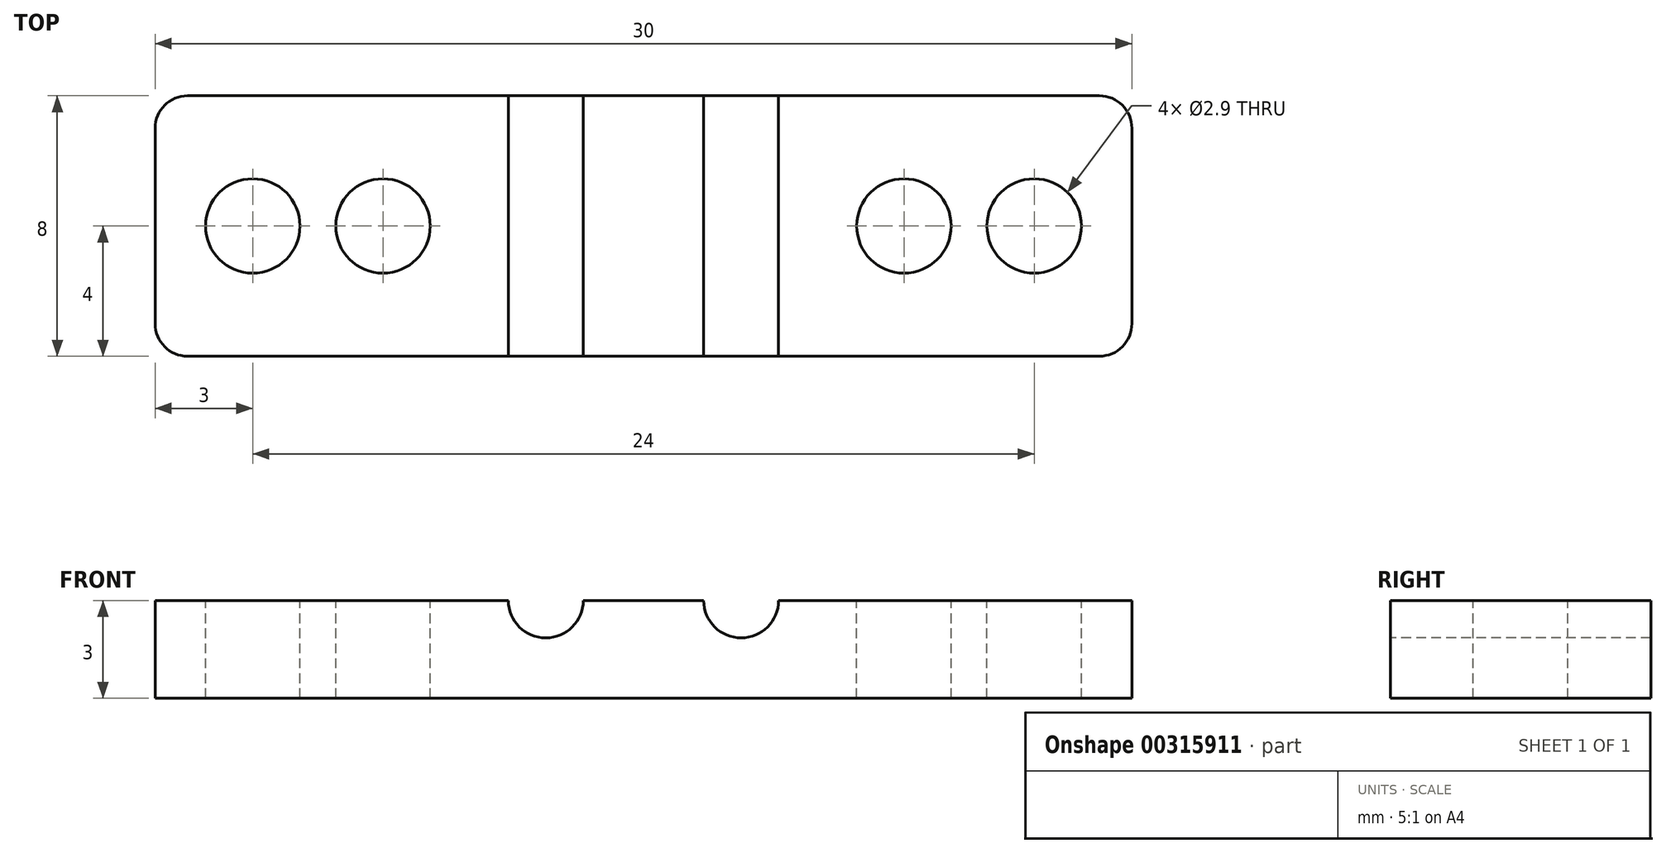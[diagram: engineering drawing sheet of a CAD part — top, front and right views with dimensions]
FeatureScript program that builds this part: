
annotation { "Feature Type Name" : "Feature", "Feature Type Description" : "" }
export const myFeature = defineFeature(function(context is Context, id is Id, definition is map)
    precondition{}
    {
        {
            var Q0;
            Q0=qCreatedBy(makeId("Top.planeOp"),FACE);
            var sketch = newSketch(context, id + "F0", { "sketchPlane" : qUnion([Q0])});
            skLineSegment(sketch, "E0.bottom", {"start": v(3, 4) * mm, "end": v(-3, 4) * mm});
            skLineSegment(sketch, "E0.top", {"start": v(3, -4) * mm, "end": v(-3, -4) * mm});
            skLineSegment(sketch, "E0.left", {"start": v(3, 4) * mm, "end": v(3, -4) * mm});
            skLineSegment(sketch, "E0.right", {"start": v(-3, 4) * mm, "end": v(-3, -4) * mm});
            skPoint(sketch, "E0.middle", {"position": v(0, 0) * mm});
            skLineSegment(sketch, "E1.bottom", {"start": v(27, 4) * mm, "end": v(21, 4) * mm});
            skLineSegment(sketch, "E1.top", {"start": v(27, -4) * mm, "end": v(21, -4) * mm});
            skLineSegment(sketch, "E1.left", {"start": v(27, 4) * mm, "end": v(27, -4) * mm});
            skLineSegment(sketch, "E1.right", {"start": v(21, 4) * mm, "end": v(21, -4) * mm});
            skPoint(sketch, "E1.middle", {"position": v(24, 0) * mm});
            skLineSegment(sketch, "E2", {"start": v(3, 4) * mm, "end": v(21, 4) * mm});
            skLineSegment(sketch, "E3", {"start": v(3, -4) * mm, "end": v(21, -4) * mm});
            skLineSegment(sketch, "E4", {"start": v(9, 4) * mm, "end": v(9, -4) * mm, "construction": true});
            skLineSegment(sketch, "E5.1.0.0", {"start": v(15, 4) * mm, "end": v(15, -4) * mm, "construction": true});
            skLineSegment(sketch, "E5.direction1", {"start": v(9, -4) * mm, "end": v(15, -4) * mm, "construction": true});
            skPoint(sketch, "E6", {"position": v(4, 0) * mm});
            skPoint(sketch, "E6.positionSnap0", {"position": v(3, 0) * mm});
            skPoint(sketch, "E7", {"position": v(20, 0) * mm});
            skPoint(sketch, "E7.positionSnap0", {"position": v(21, 0) * mm});
            skSolve(sketch);
        }
        {
            var Q0;
            Q0=makeQuery(id+"F0.imprint","IMPRINT",FACE,{"disambiguationData":[TD([[makeQuery(id+"F0.imprint","IMPRINT",EDGE,{"derivedFrom":sQuery(id+"F0.wireOp",EDGE,"E0.bottom")}),1.0]])]});
            var Q1;
            Q1=makeQuery(id+"F0.imprint","IMPRINT",FACE,{"disambiguationData":[TD([[makeQuery(id+"F0.imprint","IMPRINT",EDGE,{"derivedFrom":sQuery(id+"F0.wireOp",EDGE,"E0.left")}),1.0]])]});
            var Q2;
            Q2=makeQuery(id+"F0.imprint","IMPRINT",FACE,{"disambiguationData":[TD([[makeQuery(id+"F0.imprint","IMPRINT",EDGE,{"derivedFrom":sQuery(id+"F0.wireOp",EDGE,"E1.bottom")}),1.0]])]});
            extrude(context, id + "F1", {"entities" : qUnion([Q0, Q1, Q2]), "oppositeDirection" : true, "depth" : 3 * mm});
        }
        {
            var Q0;
            Q0=sQuery(id+"F0.wireOp",VERTEX,"E0.middle");
            var Q1;
            Q1=sQuery(id+"F0.wireOp",VERTEX,"E6");
            var Q2;
            Q2=sQuery(id+"F0.wireOp",VERTEX,"E7");
            var Q3;
            Q3=sQuery(id+"F0.wireOp",VERTEX,"E1.middle");
            var Q4;
            Q4=makeQuery(id+"F1.opExtrude","SWEPT_BODY",BODY,{"disambiguationData":[OSD([sQuery(id+"F0.wireOp",EDGE,"E0.bottom"),sQuery(id+"F0.wireOp",EDGE,"E0.top"),sQuery(id+"F0.wireOp",EDGE,"E0.right"),sQuery(id+"F0.wireOp",EDGE,"E1.bottom"),sQuery(id+"F0.wireOp",EDGE,"E1.top"),sQuery(id+"F0.wireOp",EDGE,"E1.left"),sQuery(id+"F0.wireOp",EDGE,"E2"),sQuery(id+"F0.wireOp",EDGE,"E3")])]});
            hole(context, id + "F2", {"style" : HoleStyle.SIMPLE, "endStyle" : HoleEndStyle.THROUGH, "holeDiameter" : 2.9 * mm, "tappedDepth" : 12 * mm, "tapClearance" : 3, "locations" : qUnion([Q0, Q1, Q2, Q3]), "scope" : qUnion([Q4])});
        }
        {
            var Q0;
            {var subQ0=sQuery(id+"F0.wireOp",EDGE,"E3");var subQ1=sQuery(id+"F0.wireOp",EDGE,"E1.top");var subQ2=sQuery(id+"F0.wireOp",EDGE,"E0.top");Q0=makeQuery(id+"FaaVOSY5iOmgxNq_1.boolean.opBoolean","MERGE",FACE,{"derivedFrom":[makeQuery(id+"F1.opExtrude","SWEPT_FACE",FACE,{"disambiguationData":[OSD([subQ2,subQ1,subQ0])]}),makeQuery(id+"FaaVOSY5iOmgxNq_1.opExtrude","SWEPT_FACE",FACE,{"disambiguationData":[OSD([subQ2,subQ1,subQ0])]})]});}
            var sketch = newSketch(context, id + "F3", { "sketchPlane" : qUnion([Q0])});
            skPoint(sketch, "E8", {"position": v(9, 0) * mm});
            skPoint(sketch, "E9.1.0.0", {"position": v(15, 0) * mm});
            skLineSegment(sketch, "E9.direction1", {"start": v(9, 0) * mm, "end": v(15, 0) * mm, "construction": true});
            skSolve(sketch);
        }
        {
            var Q0;
            Q0=sQuery(id+"F3.wireOp",VERTEX,"E8");
            var Q1;
            Q1=sQuery(id+"F3.wireOp",VERTEX,"E9.1.0.0");
            var Q2;
            Q2=makeQuery(id+"F1.opExtrude","SWEPT_BODY",BODY,{"disambiguationData":[OSD([sQuery(id+"F0.wireOp",EDGE,"E0.bottom"),sQuery(id+"F0.wireOp",EDGE,"E0.top"),sQuery(id+"F0.wireOp",EDGE,"E0.right"),sQuery(id+"F0.wireOp",EDGE,"E1.bottom"),sQuery(id+"F0.wireOp",EDGE,"E1.top"),sQuery(id+"F0.wireOp",EDGE,"E1.left"),sQuery(id+"F0.wireOp",EDGE,"E2"),sQuery(id+"F0.wireOp",EDGE,"E3")])]});
            hole(context, id + "F4", {"style" : HoleStyle.SIMPLE, "endStyle" : HoleEndStyle.THROUGH, "holeDiameter" : 2.3 * mm, "tappedDepth" : 12 * mm, "tapClearance" : 3, "locations" : qUnion([Q0, Q1]), "scope" : qUnion([Q2])});
        }
        {
            var Q0;
            Q0=makeQuery(id+"F1.opExtrude","SWEPT_EDGE",EDGE,{"disambiguationData":[OSD([sQuery(id+"F0.wireOp",EDGE,"E0.top"),sQuery(id+"F0.wireOp",EDGE,"E0.right")])]});
            var Q1;
            Q1=makeQuery(id+"F1.opExtrude","SWEPT_EDGE",EDGE,{"disambiguationData":[OSD([sQuery(id+"F0.wireOp",EDGE,"E1.top"),sQuery(id+"F0.wireOp",EDGE,"E1.left")])]});
            var Q2;
            Q2=makeQuery(id+"F1.opExtrude","SWEPT_EDGE",EDGE,{"disambiguationData":[OSD([sQuery(id+"F0.wireOp",EDGE,"E1.bottom"),sQuery(id+"F0.wireOp",EDGE,"E1.left")])]});
            var Q3;
            Q3=makeQuery(id+"F1.opExtrude","SWEPT_EDGE",EDGE,{"disambiguationData":[OSD([sQuery(id+"F0.wireOp",EDGE,"E0.bottom"),sQuery(id+"F0.wireOp",EDGE,"E0.right")])]});
            fillet(context, id + "F5", {"entities" : qUnion([Q0, Q1, Q2, Q3]), "radius" : 1 * mm, "tangentPropagation" : true, "allowEdgeOverflow" : false});
        }
    });
